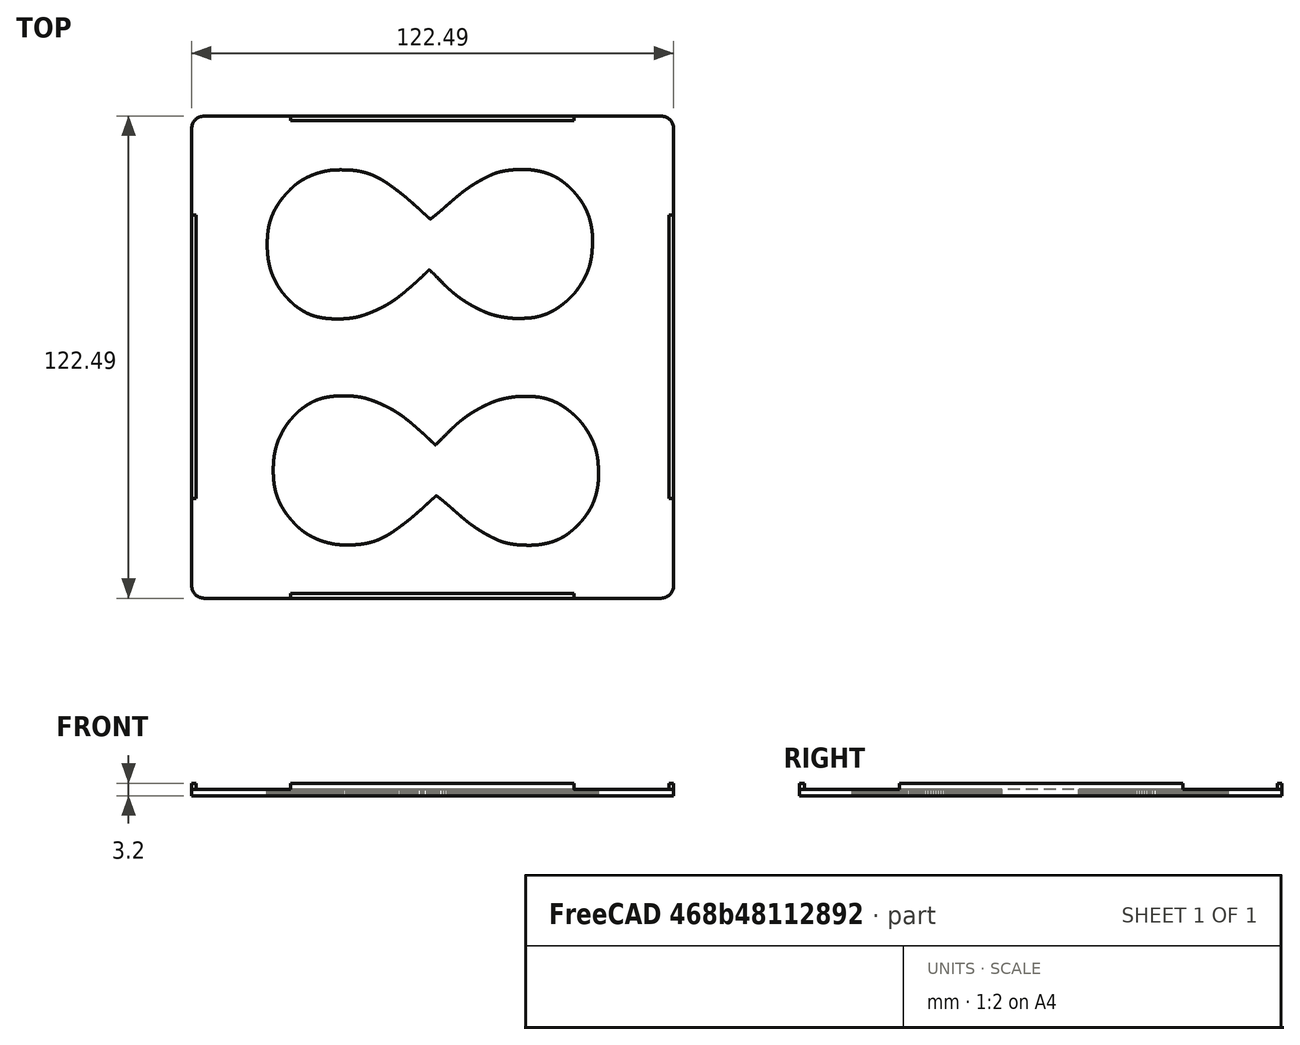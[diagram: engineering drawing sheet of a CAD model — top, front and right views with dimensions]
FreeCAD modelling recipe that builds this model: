
FCSTD DOCUMENT  (FreeCAD 0.21RUnknown)
Label: StencilCase
License: All rights reserved
LicenseURL: https://en.wikipedia.org/wiki/All_rights_reserved
objects: Part::Feature×3, Sketcher::SketchObject×3, PartDesign::Pad×2, PartDesign::Fillet×2, PartDesign::Pocket×1, PartDesign::Body×1, Mesh::Feature×1
note: 17 computed .brp shape members not serialized (recipe doc carries the construction recipe); baked Part::Feature solids carry a one-line shape summary decoded from their .brp

FEATURE [Part::Feature] rect141
  shape: bbox 120.1 x 120.1 x 2e-07 mm, 1 faces, 0 solids (baked)
FEATURE [Part::Feature] path1_5
  shape: bbox 82.66 x 37.97 x 2e-07 mm, 0 faces, 0 solids (baked)
FEATURE [Part::Feature] path1_3
  shape: bbox 82.66 x 37.97 x 2e-07 mm, 0 faces, 0 solids (baked)
FEATURE [Sketcher::SketchObject] Sketch
  FullyConstrained = false
  sketch-geometry (788):
    g0: BSplineCurve PolesCount=2 KnotsCount=2 Degree=1 IsPeriodic=0
    g1: BSplineCurve PolesCount=2 KnotsCount=2 Degree=1 IsPeriodic=0
    g2: BSplineCurve PolesCount=2 KnotsCount=2 Degree=1 IsPeriodic=0
    g3: BSplineCurve PolesCount=2 KnotsCount=2 Degree=1 IsPeriodic=0
    g4: BSplineCurve PolesCount=2 KnotsCount=2 Degree=1 IsPeriodic=0
    g5: BSplineCurve PolesCount=2 KnotsCount=2 Degree=1 IsPeriodic=0
    g6: BSplineCurve PolesCount=2 KnotsCount=2 Degree=1 IsPeriodic=0
    g7: BSplineCurve PolesCount=2 KnotsCount=2 Degree=1 IsPeriodic=0
    g8: BSplineCurve PolesCount=2 KnotsCount=2 Degree=1 IsPeriodic=0
    g9: BSplineCurve PolesCount=2 KnotsCount=2 Degree=1 IsPeriodic=0
    g10: BSplineCurve PolesCount=2 KnotsCount=2 Degree=1 IsPeriodic=0
    g11: BSplineCurve PolesCount=2 KnotsCount=2 Degree=1 IsPeriodic=0
    g12: BSplineCurve PolesCount=2 KnotsCount=2 Degree=1 IsPeriodic=0
    g13: BSplineCurve PolesCount=2 KnotsCount=2 Degree=1 IsPeriodic=0
    g14: BSplineCurve PolesCount=2 KnotsCount=2 Degree=1 IsPeriodic=0
    g15: BSplineCurve PolesCount=2 KnotsCount=2 Degree=1 IsPeriodic=0
    g16: BSplineCurve PolesCount=2 KnotsCount=2 Degree=1 IsPeriodic=0
    g17: BSplineCurve PolesCount=2 KnotsCount=2 Degree=1 IsPeriodic=0
    g18: BSplineCurve PolesCount=2 KnotsCount=2 Degree=1 IsPeriodic=0
    g19: BSplineCurve PolesCount=2 KnotsCount=2 Degree=1 IsPeriodic=0
    g20: BSplineCurve PolesCount=2 KnotsCount=2 Degree=1 IsPeriodic=0
    g21: BSplineCurve PolesCount=2 KnotsCount=2 Degree=1 IsPeriodic=0
    g22: BSplineCurve PolesCount=2 KnotsCount=2 Degree=1 IsPeriodic=0
    g23: BSplineCurve PolesCount=2 KnotsCount=2 Degree=1 IsPeriodic=0
    g24: BSplineCurve PolesCount=2 KnotsCount=2 Degree=1 IsPeriodic=0
    g25: BSplineCurve PolesCount=2 KnotsCount=2 Degree=1 IsPeriodic=0
    g26: BSplineCurve PolesCount=2 KnotsCount=2 Degree=1 IsPeriodic=0
    g27: BSplineCurve PolesCount=2 KnotsCount=2 Degree=1 IsPeriodic=0
    g28: BSplineCurve PolesCount=2 KnotsCount=2 Degree=1 IsPeriodic=0
    g29: BSplineCurve PolesCount=2 KnotsCount=2 Degree=1 IsPeriodic=0
    g30: BSplineCurve PolesCount=2 KnotsCount=2 Degree=1 IsPeriodic=0
    g31: BSplineCurve PolesCount=2 KnotsCount=2 Degree=1 IsPeriodic=0
    g32: BSplineCurve PolesCount=2 KnotsCount=2 Degree=1 IsPeriodic=0
    g33: BSplineCurve PolesCount=2 KnotsCount=2 Degree=1 IsPeriodic=0
    g34: BSplineCurve PolesCount=2 KnotsCount=2 Degree=1 IsPeriodic=0
    g35: BSplineCurve PolesCount=2 KnotsCount=2 Degree=1 IsPeriodic=0
    g36: BSplineCurve PolesCount=2 KnotsCount=2 Degree=1 IsPeriodic=0
    g37: BSplineCurve PolesCount=2 KnotsCount=2 Degree=1 IsPeriodic=0
    g38: BSplineCurve PolesCount=2 KnotsCount=2 Degree=1 IsPeriodic=0
    g39: BSplineCurve PolesCount=2 KnotsCount=2 Degree=1 IsPeriodic=0
    g40: BSplineCurve PolesCount=2 KnotsCount=2 Degree=1 IsPeriodic=0
    g41: BSplineCurve PolesCount=2 KnotsCount=2 Degree=1 IsPeriodic=0
    g42: BSplineCurve PolesCount=2 KnotsCount=2 Degree=1 IsPeriodic=0
    g43: BSplineCurve PolesCount=2 KnotsCount=2 Degree=1 IsPeriodic=0
    g44: BSplineCurve PolesCount=2 KnotsCount=2 Degree=1 IsPeriodic=0
    g45: BSplineCurve PolesCount=2 KnotsCount=2 Degree=1 IsPeriodic=0
    g46: BSplineCurve PolesCount=2 KnotsCount=2 Degree=1 IsPeriodic=0
    g47: BSplineCurve PolesCount=2 KnotsCount=2 Degree=1 IsPeriodic=0
    g48: BSplineCurve PolesCount=2 KnotsCount=2 Degree=1 IsPeriodic=0
    g49: BSplineCurve PolesCount=2 KnotsCount=2 Degree=1 IsPeriodic=0
    g50: BSplineCurve PolesCount=2 KnotsCount=2 Degree=1 IsPeriodic=0
    g51: BSplineCurve PolesCount=2 KnotsCount=2 Degree=1 IsPeriodic=0
    g52: BSplineCurve PolesCount=2 KnotsCount=2 Degree=1 IsPeriodic=0
    g53: BSplineCurve PolesCount=2 KnotsCount=2 Degree=1 IsPeriodic=0
    g54: BSplineCurve PolesCount=2 KnotsCount=2 Degree=1 IsPeriodic=0
    g55: BSplineCurve PolesCount=2 KnotsCount=2 Degree=1 IsPeriodic=0
    g56: BSplineCurve PolesCount=2 KnotsCount=2 Degree=1 IsPeriodic=0
    g57: BSplineCurve PolesCount=2 KnotsCount=2 Degree=1 IsPeriodic=0
    g58: BSplineCurve PolesCount=2 KnotsCount=2 Degree=1 IsPeriodic=0
    g59: BSplineCurve PolesCount=2 KnotsCount=2 Degree=1 IsPeriodic=0
    g60: BSplineCurve PolesCount=2 KnotsCount=2 Degree=1 IsPeriodic=0
    g61: BSplineCurve PolesCount=2 KnotsCount=2 Degree=1 IsPeriodic=0
    g62: BSplineCurve PolesCount=2 KnotsCount=2 Degree=1 IsPeriodic=0
    g63: BSplineCurve PolesCount=2 KnotsCount=2 Degree=1 IsPeriodic=0
    g64: BSplineCurve PolesCount=2 KnotsCount=2 Degree=1 IsPeriodic=0
    g65: BSplineCurve PolesCount=2 KnotsCount=2 Degree=1 IsPeriodic=0
    g66: BSplineCurve PolesCount=2 KnotsCount=2 Degree=1 IsPeriodic=0
    g67: BSplineCurve PolesCount=2 KnotsCount=2 Degree=1 IsPeriodic=0
    g68: BSplineCurve PolesCount=2 KnotsCount=2 Degree=1 IsPeriodic=0
    g69: BSplineCurve PolesCount=2 KnotsCount=2 Degree=1 IsPeriodic=0
    g70: BSplineCurve PolesCount=2 KnotsCount=2 Degree=1 IsPeriodic=0
    g71: BSplineCurve PolesCount=2 KnotsCount=2 Degree=1 IsPeriodic=0
    g72: BSplineCurve PolesCount=2 KnotsCount=2 Degree=1 IsPeriodic=0
    g73: BSplineCurve PolesCount=2 KnotsCount=2 Degree=1 IsPeriodic=0
    g74: BSplineCurve PolesCount=2 KnotsCount=2 Degree=1 IsPeriodic=0
    g75: BSplineCurve PolesCount=2 KnotsCount=2 Degree=1 IsPeriodic=0
    g76: BSplineCurve PolesCount=2 KnotsCount=2 Degree=1 IsPeriodic=0
    g77: BSplineCurve PolesCount=2 KnotsCount=2 Degree=1 IsPeriodic=0
    g78: BSplineCurve PolesCount=2 KnotsCount=2 Degree=1 IsPeriodic=0
    g79: BSplineCurve PolesCount=2 KnotsCount=2 Degree=1 IsPeriodic=0
    g80: BSplineCurve PolesCount=2 KnotsCount=2 Degree=1 IsPeriodic=0
    g81: BSplineCurve PolesCount=2 KnotsCount=2 Degree=1 IsPeriodic=0
    g82: BSplineCurve PolesCount=2 KnotsCount=2 Degree=1 IsPeriodic=0
    g83: BSplineCurve PolesCount=2 KnotsCount=2 Degree=1 IsPeriodic=0
    g84: BSplineCurve PolesCount=2 KnotsCount=2 Degree=1 IsPeriodic=0
    g85: BSplineCurve PolesCount=2 KnotsCount=2 Degree=1 IsPeriodic=0
    g86: BSplineCurve PolesCount=2 KnotsCount=2 Degree=1 IsPeriodic=0
    g87: BSplineCurve PolesCount=2 KnotsCount=2 Degree=1 IsPeriodic=0
    g88: BSplineCurve PolesCount=2 KnotsCount=2 Degree=1 IsPeriodic=0
    g89: BSplineCurve PolesCount=2 KnotsCount=2 Degree=1 IsPeriodic=0
    g90: BSplineCurve PolesCount=2 KnotsCount=2 Degree=1 IsPeriodic=0
    g91: BSplineCurve PolesCount=2 KnotsCount=2 Degree=1 IsPeriodic=0
    g92: BSplineCurve PolesCount=2 KnotsCount=2 Degree=1 IsPeriodic=0
    g93: BSplineCurve PolesCount=2 KnotsCount=2 Degree=1 IsPeriodic=0
    g94: BSplineCurve PolesCount=2 KnotsCount=2 Degree=1 IsPeriodic=0
    g95: BSplineCurve PolesCount=2 KnotsCount=2 Degree=1 IsPeriodic=0
    g96: BSplineCurve PolesCount=2 KnotsCount=2 Degree=1 IsPeriodic=0
    g97: BSplineCurve PolesCount=2 KnotsCount=2 Degree=1 IsPeriodic=0
    g98: BSplineCurve PolesCount=2 KnotsCount=2 Degree=1 IsPeriodic=0
    g99: BSplineCurve PolesCount=2 KnotsCount=2 Degree=1 IsPeriodic=0
    g100: BSplineCurve PolesCount=2 KnotsCount=2 Degree=1 IsPeriodic=0
    g101: BSplineCurve PolesCount=2 KnotsCount=2 Degree=1 IsPeriodic=0
    g102: BSplineCurve PolesCount=2 KnotsCount=2 Degree=1 IsPeriodic=0
    g103: BSplineCurve PolesCount=2 KnotsCount=2 Degree=1 IsPeriodic=0
    g104: BSplineCurve PolesCount=2 KnotsCount=2 Degree=1 IsPeriodic=0
    g105: BSplineCurve PolesCount=2 KnotsCount=2 Degree=1 IsPeriodic=0
    g106: BSplineCurve PolesCount=2 KnotsCount=2 Degree=1 IsPeriodic=0
    g107: BSplineCurve PolesCount=2 KnotsCount=2 Degree=1 IsPeriodic=0
    g108: BSplineCurve PolesCount=2 KnotsCount=2 Degree=1 IsPeriodic=0
    g109: BSplineCurve PolesCount=2 KnotsCount=2 Degree=1 IsPeriodic=0
    g110: BSplineCurve PolesCount=2 KnotsCount=2 Degree=1 IsPeriodic=0
    g111: BSplineCurve PolesCount=2 KnotsCount=2 Degree=1 IsPeriodic=0
    g112: BSplineCurve PolesCount=2 KnotsCount=2 Degree=1 IsPeriodic=0
    g113: BSplineCurve PolesCount=2 KnotsCount=2 Degree=1 IsPeriodic=0
    g114: BSplineCurve PolesCount=2 KnotsCount=2 Degree=1 IsPeriodic=0
    g115: BSplineCurve PolesCount=2 KnotsCount=2 Degree=1 IsPeriodic=0
    g116: BSplineCurve PolesCount=2 KnotsCount=2 Degree=1 IsPeriodic=0
    g117: BSplineCurve PolesCount=2 KnotsCount=2 Degree=1 IsPeriodic=0
    g118: BSplineCurve PolesCount=2 KnotsCount=2 Degree=1 IsPeriodic=0
    g119: BSplineCurve PolesCount=2 KnotsCount=2 Degree=1 IsPeriodic=0
    g120: BSplineCurve PolesCount=2 KnotsCount=2 Degree=1 IsPeriodic=0
    g121: BSplineCurve PolesCount=2 KnotsCount=2 Degree=1 IsPeriodic=0
    g122: BSplineCurve PolesCount=2 KnotsCount=2 Degree=1 IsPeriodic=0
    g123: BSplineCurve PolesCount=2 KnotsCount=2 Degree=1 IsPeriodic=0
    g124: BSplineCurve PolesCount=2 KnotsCount=2 Degree=1 IsPeriodic=0
    g125: BSplineCurve PolesCount=2 KnotsCount=2 Degree=1 IsPeriodic=0
    g126: BSplineCurve PolesCount=2 KnotsCount=2 Degree=1 IsPeriodic=0
    g127: BSplineCurve PolesCount=2 KnotsCount=2 Degree=1 IsPeriodic=0
    g128: BSplineCurve PolesCount=2 KnotsCount=2 Degree=1 IsPeriodic=0
    g129: BSplineCurve PolesCount=2 KnotsCount=2 Degree=1 IsPeriodic=0
    g130: BSplineCurve PolesCount=2 KnotsCount=2 Degree=1 IsPeriodic=0
    g131: BSplineCurve PolesCount=2 KnotsCount=2 Degree=1 IsPeriodic=0
    g132: BSplineCurve PolesCount=2 KnotsCount=2 Degree=1 IsPeriodic=0
    g133: BSplineCurve PolesCount=2 KnotsCount=2 Degree=1 IsPeriodic=0
    g134: BSplineCurve PolesCount=2 KnotsCount=2 Degree=1 IsPeriodic=0
    g135: BSplineCurve PolesCount=2 KnotsCount=2 Degree=1 IsPeriodic=0
    g136: BSplineCurve PolesCount=2 KnotsCount=2 Degree=1 IsPeriodic=0
    g137: BSplineCurve PolesCount=2 KnotsCount=2 Degree=1 IsPeriodic=0
    g138: BSplineCurve PolesCount=2 KnotsCount=2 Degree=1 IsPeriodic=0
    g139: BSplineCurve PolesCount=2 KnotsCount=2 Degree=1 IsPeriodic=0
    g140: BSplineCurve PolesCount=2 KnotsCount=2 Degree=1 IsPeriodic=0
    g141: BSplineCurve PolesCount=2 KnotsCount=2 Degree=1 IsPeriodic=0
    g142: BSplineCurve PolesCount=2 KnotsCount=2 Degree=1 IsPeriodic=0
    g143: BSplineCurve PolesCount=2 KnotsCount=2 Degree=1 IsPeriodic=0
    g144: BSplineCurve PolesCount=2 KnotsCount=2 Degree=1 IsPeriodic=0
    g145: BSplineCurve PolesCount=2 KnotsCount=2 Degree=1 IsPeriodic=0
    g146: BSplineCurve PolesCount=2 KnotsCount=2 Degree=1 IsPeriodic=0
    g147: BSplineCurve PolesCount=2 KnotsCount=2 Degree=1 IsPeriodic=0
    g148: BSplineCurve PolesCount=2 KnotsCount=2 Degree=1 IsPeriodic=0
    g149: BSplineCurve PolesCount=2 KnotsCount=2 Degree=1 IsPeriodic=0
    g150: BSplineCurve PolesCount=2 KnotsCount=2 Degree=1 IsPeriodic=0
    g151: BSplineCurve PolesCount=2 KnotsCount=2 Degree=1 IsPeriodic=0
    g152: BSplineCurve PolesCount=2 KnotsCount=2 Degree=1 IsPeriodic=0
    g153: BSplineCurve PolesCount=2 KnotsCount=2 Degree=1 IsPeriodic=0
    g154: BSplineCurve PolesCount=2 KnotsCount=2 Degree=1 IsPeriodic=0
    g155: BSplineCurve PolesCount=2 KnotsCount=2 Degree=1 IsPeriodic=0
    g156: BSplineCurve PolesCount=2 KnotsCount=2 Degree=1 IsPeriodic=0
    g157: BSplineCurve PolesCount=2 KnotsCount=2 Degree=1 IsPeriodic=0
    g158: BSplineCurve PolesCount=2 KnotsCount=2 Degree=1 IsPeriodic=0
    g159: BSplineCurve PolesCount=2 KnotsCount=2 Degree=1 IsPeriodic=0
    g160: BSplineCurve PolesCount=2 KnotsCount=2 Degree=1 IsPeriodic=0
    g161: BSplineCurve PolesCount=2 KnotsCount=2 Degree=1 IsPeriodic=0
    g162: BSplineCurve PolesCount=2 KnotsCount=2 Degree=1 IsPeriodic=0
    g163: BSplineCurve PolesCount=2 KnotsCount=2 Degree=1 IsPeriodic=0
    g164: BSplineCurve PolesCount=2 KnotsCount=2 Degree=1 IsPeriodic=0
    g165: BSplineCurve PolesCount=2 KnotsCount=2 Degree=1 IsPeriodic=0
    g166: BSplineCurve PolesCount=2 KnotsCount=2 Degree=1 IsPeriodic=0
    g167: BSplineCurve PolesCount=2 KnotsCount=2 Degree=1 IsPeriodic=0
    g168: BSplineCurve PolesCount=2 KnotsCount=2 Degree=1 IsPeriodic=0
    g169: BSplineCurve PolesCount=2 KnotsCount=2 Degree=1 IsPeriodic=0
    g170: BSplineCurve PolesCount=2 KnotsCount=2 Degree=1 IsPeriodic=0
    g171: BSplineCurve PolesCount=2 KnotsCount=2 Degree=1 IsPeriodic=0
    g172: BSplineCurve PolesCount=2 KnotsCount=2 Degree=1 IsPeriodic=0
    g173: BSplineCurve PolesCount=2 KnotsCount=2 Degree=1 IsPeriodic=0
    g174: BSplineCurve PolesCount=2 KnotsCount=2 Degree=1 IsPeriodic=0
    g175: BSplineCurve PolesCount=2 KnotsCount=2 Degree=1 IsPeriodic=0
    g176: BSplineCurve PolesCount=2 KnotsCount=2 Degree=1 IsPeriodic=0
    g177: BSplineCurve PolesCount=2 KnotsCount=2 Degree=1 IsPeriodic=0
    g178: BSplineCurve PolesCount=2 KnotsCount=2 Degree=1 IsPeriodic=0
    g179: BSplineCurve PolesCount=2 KnotsCount=2 Degree=1 IsPeriodic=0
    g180: BSplineCurve PolesCount=2 KnotsCount=2 Degree=1 IsPeriodic=0
    g181: BSplineCurve PolesCount=2 KnotsCount=2 Degree=1 IsPeriodic=0
    g182: BSplineCurve PolesCount=2 KnotsCount=2 Degree=1 IsPeriodic=0
    g183: BSplineCurve PolesCount=2 KnotsCount=2 Degree=1 IsPeriodic=0
    g184: BSplineCurve PolesCount=2 KnotsCount=2 Degree=1 IsPeriodic=0
    g185: BSplineCurve PolesCount=2 KnotsCount=2 Degree=1 IsPeriodic=0
    g186: BSplineCurve PolesCount=2 KnotsCount=2 Degree=1 IsPeriodic=0
    g187: BSplineCurve PolesCount=2 KnotsCount=2 Degree=1 IsPeriodic=0
    g188: BSplineCurve PolesCount=2 KnotsCount=2 Degree=1 IsPeriodic=0
    g189: BSplineCurve PolesCount=2 KnotsCount=2 Degree=1 IsPeriodic=0
    g190: BSplineCurve PolesCount=2 KnotsCount=2 Degree=1 IsPeriodic=0
    g191: BSplineCurve PolesCount=2 KnotsCount=2 Degree=1 IsPeriodic=0
    g192: BSplineCurve PolesCount=2 KnotsCount=2 Degree=1 IsPeriodic=0
    g193: BSplineCurve PolesCount=2 KnotsCount=2 Degree=1 IsPeriodic=0
    g194: BSplineCurve PolesCount=2 KnotsCount=2 Degree=1 IsPeriodic=0
    g195: BSplineCurve PolesCount=2 KnotsCount=2 Degree=1 IsPeriodic=0
    g196: BSplineCurve PolesCount=2 KnotsCount=2 Degree=1 IsPeriodic=0
    g197: BSplineCurve PolesCount=2 KnotsCount=2 Degree=1 IsPeriodic=0
    g198: BSplineCurve PolesCount=2 KnotsCount=2 Degree=1 IsPeriodic=0
    g199: BSplineCurve PolesCount=2 KnotsCount=2 Degree=1 IsPeriodic=0
    g200: BSplineCurve PolesCount=2 KnotsCount=2 Degree=1 IsPeriodic=0
    g201: BSplineCurve PolesCount=2 KnotsCount=2 Degree=1 IsPeriodic=0
    g202: BSplineCurve PolesCount=2 KnotsCount=2 Degree=1 IsPeriodic=0
    g203: BSplineCurve PolesCount=2 KnotsCount=2 Degree=1 IsPeriodic=0
    g204: BSplineCurve PolesCount=2 KnotsCount=2 Degree=1 IsPeriodic=0
    g205: BSplineCurve PolesCount=2 KnotsCount=2 Degree=1 IsPeriodic=0
    g206: BSplineCurve PolesCount=2 KnotsCount=2 Degree=1 IsPeriodic=0
    g207: BSplineCurve PolesCount=2 KnotsCount=2 Degree=1 IsPeriodic=0
    g208: BSplineCurve PolesCount=2 KnotsCount=2 Degree=1 IsPeriodic=0
    g209: BSplineCurve PolesCount=2 KnotsCount=2 Degree=1 IsPeriodic=0
    g210: BSplineCurve PolesCount=2 KnotsCount=2 Degree=1 IsPeriodic=0
    g211: BSplineCurve PolesCount=2 KnotsCount=2 Degree=1 IsPeriodic=0
    g212: BSplineCurve PolesCount=2 KnotsCount=2 Degree=1 IsPeriodic=0
    g213: BSplineCurve PolesCount=2 KnotsCount=2 Degree=1 IsPeriodic=0
    g214: BSplineCurve PolesCount=2 KnotsCount=2 Degree=1 IsPeriodic=0
    g215: BSplineCurve PolesCount=2 KnotsCount=2 Degree=1 IsPeriodic=0
    g216: BSplineCurve PolesCount=2 KnotsCount=2 Degree=1 IsPeriodic=0
    g217: BSplineCurve PolesCount=2 KnotsCount=2 Degree=1 IsPeriodic=0
    g218: BSplineCurve PolesCount=2 KnotsCount=2 Degree=1 IsPeriodic=0
    g219: BSplineCurve PolesCount=2 KnotsCount=2 Degree=1 IsPeriodic=0
    g220: BSplineCurve PolesCount=2 KnotsCount=2 Degree=1 IsPeriodic=0
    g221: BSplineCurve PolesCount=2 KnotsCount=2 Degree=1 IsPeriodic=0
    g222: BSplineCurve PolesCount=2 KnotsCount=2 Degree=1 IsPeriodic=0
    g223: BSplineCurve PolesCount=2 KnotsCount=2 Degree=1 IsPeriodic=0
    g224: BSplineCurve PolesCount=2 KnotsCount=2 Degree=1 IsPeriodic=0
    g225: BSplineCurve PolesCount=2 KnotsCount=2 Degree=1 IsPeriodic=0
    g226: BSplineCurve PolesCount=2 KnotsCount=2 Degree=1 IsPeriodic=0
    g227: BSplineCurve PolesCount=2 KnotsCount=2 Degree=1 IsPeriodic=0
    g228: BSplineCurve PolesCount=2 KnotsCount=2 Degree=1 IsPeriodic=0
    g229: BSplineCurve PolesCount=2 KnotsCount=2 Degree=1 IsPeriodic=0
    g230: BSplineCurve PolesCount=2 KnotsCount=2 Degree=1 IsPeriodic=0
    g231: BSplineCurve PolesCount=2 KnotsCount=2 Degree=1 IsPeriodic=0
    g232: BSplineCurve PolesCount=2 KnotsCount=2 Degree=1 IsPeriodic=0
    g233: BSplineCurve PolesCount=2 KnotsCount=2 Degree=1 IsPeriodic=0
    g234: BSplineCurve PolesCount=2 KnotsCount=2 Degree=1 IsPeriodic=0
    g235: BSplineCurve PolesCount=2 KnotsCount=2 Degree=1 IsPeriodic=0
    g236: BSplineCurve PolesCount=2 KnotsCount=2 Degree=1 IsPeriodic=0
    g237: BSplineCurve PolesCount=2 KnotsCount=2 Degree=1 IsPeriodic=0
    g238: BSplineCurve PolesCount=2 KnotsCount=2 Degree=1 IsPeriodic=0
    g239: BSplineCurve PolesCount=2 KnotsCount=2 Degree=1 IsPeriodic=0
    g240: BSplineCurve PolesCount=2 KnotsCount=2 Degree=1 IsPeriodic=0
    g241: BSplineCurve PolesCount=2 KnotsCount=2 Degree=1 IsPeriodic=0
    g242: BSplineCurve PolesCount=2 KnotsCount=2 Degree=1 IsPeriodic=0
    g243: BSplineCurve PolesCount=2 KnotsCount=2 Degree=1 IsPeriodic=0
    g244: BSplineCurve PolesCount=2 KnotsCount=2 Degree=1 IsPeriodic=0
    g245: BSplineCurve PolesCount=2 KnotsCount=2 Degree=1 IsPeriodic=0
    g246: BSplineCurve PolesCount=2 KnotsCount=2 Degree=1 IsPeriodic=0
    g247: BSplineCurve PolesCount=2 KnotsCount=2 Degree=1 IsPeriodic=0
    g248: BSplineCurve PolesCount=2 KnotsCount=2 Degree=1 IsPeriodic=0
    g249: BSplineCurve PolesCount=2 KnotsCount=2 Degree=1 IsPeriodic=0
    g250: BSplineCurve PolesCount=2 KnotsCount=2 Degree=1 IsPeriodic=0
    g251: BSplineCurve PolesCount=2 KnotsCount=2 Degree=1 IsPeriodic=0
    g252: BSplineCurve PolesCount=2 KnotsCount=2 Degree=1 IsPeriodic=0
    g253: BSplineCurve PolesCount=2 KnotsCount=2 Degree=1 IsPeriodic=0
    g254: BSplineCurve PolesCount=2 KnotsCount=2 Degree=1 IsPeriodic=0
    g255: BSplineCurve PolesCount=2 KnotsCount=2 Degree=1 IsPeriodic=0
    g256: BSplineCurve PolesCount=2 KnotsCount=2 Degree=1 IsPeriodic=0
    g257: BSplineCurve PolesCount=2 KnotsCount=2 Degree=1 IsPeriodic=0
    g258: BSplineCurve PolesCount=2 KnotsCount=2 Degree=1 IsPeriodic=0
    g259: BSplineCurve PolesCount=2 KnotsCount=2 Degree=1 IsPeriodic=0
    g260: BSplineCurve PolesCount=2 KnotsCount=2 Degree=1 IsPeriodic=0
    g261: BSplineCurve PolesCount=2 KnotsCount=2 Degree=1 IsPeriodic=0
    g262: BSplineCurve PolesCount=2 KnotsCount=2 Degree=1 IsPeriodic=0
    g263: BSplineCurve PolesCount=2 KnotsCount=2 Degree=1 IsPeriodic=0
    g264: BSplineCurve PolesCount=2 KnotsCount=2 Degree=1 IsPeriodic=0
    g265: BSplineCurve PolesCount=2 KnotsCount=2 Degree=1 IsPeriodic=0
    g266: BSplineCurve PolesCount=2 KnotsCount=2 Degree=1 IsPeriodic=0
    g267: BSplineCurve PolesCount=2 KnotsCount=2 Degree=1 IsPeriodic=0
    g268: BSplineCurve PolesCount=2 KnotsCount=2 Degree=1 IsPeriodic=0
    g269: BSplineCurve PolesCount=2 KnotsCount=2 Degree=1 IsPeriodic=0
    g270: BSplineCurve PolesCount=2 KnotsCount=2 Degree=1 IsPeriodic=0
    g271: BSplineCurve PolesCount=2 KnotsCount=2 Degree=1 IsPeriodic=0
    g272: BSplineCurve PolesCount=2 KnotsCount=2 Degree=1 IsPeriodic=0
    g273: BSplineCurve PolesCount=2 KnotsCount=2 Degree=1 IsPeriodic=0
    g274: BSplineCurve PolesCount=2 KnotsCount=2 Degree=1 IsPeriodic=0
    g275: BSplineCurve PolesCount=2 KnotsCount=2 Degree=1 IsPeriodic=0
    g276: BSplineCurve PolesCount=2 KnotsCount=2 Degree=1 IsPeriodic=0
    g277: BSplineCurve PolesCount=2 KnotsCount=2 Degree=1 IsPeriodic=0
    g278: BSplineCurve PolesCount=2 KnotsCount=2 Degree=1 IsPeriodic=0
    g279: BSplineCurve PolesCount=2 KnotsCount=2 Degree=1 IsPeriodic=0
    g280: BSplineCurve PolesCount=2 KnotsCount=2 Degree=1 IsPeriodic=0
    g281: BSplineCurve PolesCount=2 KnotsCount=2 Degree=1 IsPeriodic=0
    g282: BSplineCurve PolesCount=2 KnotsCount=2 Degree=1 IsPeriodic=0
    g283: BSplineCurve PolesCount=2 KnotsCount=2 Degree=1 IsPeriodic=0
    g284: BSplineCurve PolesCount=2 KnotsCount=2 Degree=1 IsPeriodic=0
    g285: BSplineCurve PolesCount=2 KnotsCount=2 Degree=1 IsPeriodic=0
    g286: BSplineCurve PolesCount=2 KnotsCount=2 Degree=1 IsPeriodic=0
    g287: BSplineCurve PolesCount=2 KnotsCount=2 Degree=1 IsPeriodic=0
    g288: BSplineCurve PolesCount=2 KnotsCount=2 Degree=1 IsPeriodic=0
    g289: BSplineCurve PolesCount=2 KnotsCount=2 Degree=1 IsPeriodic=0
    g290: BSplineCurve PolesCount=2 KnotsCount=2 Degree=1 IsPeriodic=0
    g291: BSplineCurve PolesCount=2 KnotsCount=2 Degree=1 IsPeriodic=0
    g292: BSplineCurve PolesCount=2 KnotsCount=2 Degree=1 IsPeriodic=0
    g293: BSplineCurve PolesCount=2 KnotsCount=2 Degree=1 IsPeriodic=0
    g294: BSplineCurve PolesCount=2 KnotsCount=2 Degree=1 IsPeriodic=0
    g295: BSplineCurve PolesCount=2 KnotsCount=2 Degree=1 IsPeriodic=0
    g296: BSplineCurve PolesCount=2 KnotsCount=2 Degree=1 IsPeriodic=0
    g297: BSplineCurve PolesCount=2 KnotsCount=2 Degree=1 IsPeriodic=0
    g298: BSplineCurve PolesCount=2 KnotsCount=2 Degree=1 IsPeriodic=0
    g299: BSplineCurve PolesCount=2 KnotsCount=2 Degree=1 IsPeriodic=0
    g300: BSplineCurve PolesCount=2 KnotsCount=2 Degree=1 IsPeriodic=0
    g301: BSplineCurve PolesCount=2 KnotsCount=2 Degree=1 IsPeriodic=0
    g302: BSplineCurve PolesCount=2 KnotsCount=2 Degree=1 IsPeriodic=0
    g303: BSplineCurve PolesCount=2 KnotsCount=2 Degree=1 IsPeriodic=0
    g304: BSplineCurve PolesCount=2 KnotsCount=2 Degree=1 IsPeriodic=0
    g305: BSplineCurve PolesCount=2 KnotsCount=2 Degree=1 IsPeriodic=0
    g306: BSplineCurve PolesCount=2 KnotsCount=2 Degree=1 IsPeriodic=0
    g307: BSplineCurve PolesCount=2 KnotsCount=2 Degree=1 IsPeriodic=0
    g308: BSplineCurve PolesCount=2 KnotsCount=2 Degree=1 IsPeriodic=0
    g309: BSplineCurve PolesCount=2 KnotsCount=2 Degree=1 IsPeriodic=0
    g310: BSplineCurve PolesCount=2 KnotsCount=2 Degree=1 IsPeriodic=0
    g311: BSplineCurve PolesCount=2 KnotsCount=2 Degree=1 IsPeriodic=0
    g312: BSplineCurve PolesCount=2 KnotsCount=2 Degree=1 IsPeriodic=0
    g313: BSplineCurve PolesCount=2 KnotsCount=2 Degree=1 IsPeriodic=0
    g314: BSplineCurve PolesCount=2 KnotsCount=2 Degree=1 IsPeriodic=0
    g315: BSplineCurve PolesCount=2 KnotsCount=2 Degree=1 IsPeriodic=0
    g316: BSplineCurve PolesCount=2 KnotsCount=2 Degree=1 IsPeriodic=0
    g317: BSplineCurve PolesCount=2 KnotsCount=2 Degree=1 IsPeriodic=0
    g318: BSplineCurve PolesCount=2 KnotsCount=2 Degree=1 IsPeriodic=0
    g319: BSplineCurve PolesCount=2 KnotsCount=2 Degree=1 IsPeriodic=0
    g320: BSplineCurve PolesCount=2 KnotsCount=2 Degree=1 IsPeriodic=0
    g321: BSplineCurve PolesCount=2 KnotsCount=2 Degree=1 IsPeriodic=0
    g322: BSplineCurve PolesCount=2 KnotsCount=2 Degree=1 IsPeriodic=0
    g323: BSplineCurve PolesCount=2 KnotsCount=2 Degree=1 IsPeriodic=0
    g324: BSplineCurve PolesCount=2 KnotsCount=2 Degree=1 IsPeriodic=0
    g325: BSplineCurve PolesCount=2 KnotsCount=2 Degree=1 IsPeriodic=0
    g326: BSplineCurve PolesCount=2 KnotsCount=2 Degree=1 IsPeriodic=0
    g327: BSplineCurve PolesCount=2 KnotsCount=2 Degree=1 IsPeriodic=0
    g328: BSplineCurve PolesCount=2 KnotsCount=2 Degree=1 IsPeriodic=0
    g329: BSplineCurve PolesCount=2 KnotsCount=2 Degree=1 IsPeriodic=0
    g330: BSplineCurve PolesCount=2 KnotsCount=2 Degree=1 IsPeriodic=0
    g331: BSplineCurve PolesCount=2 KnotsCount=2 Degree=1 IsPeriodic=0
    g332: BSplineCurve PolesCount=2 KnotsCount=2 Degree=1 IsPeriodic=0
    g333: BSplineCurve PolesCount=2 KnotsCount=2 Degree=1 IsPeriodic=0
    g334: BSplineCurve PolesCount=2 KnotsCount=2 Degree=1 IsPeriodic=0
    g335: BSplineCurve PolesCount=2 KnotsCount=2 Degree=1 IsPeriodic=0
    g336: BSplineCurve PolesCount=2 KnotsCount=2 Degree=1 IsPeriodic=0
    g337: BSplineCurve PolesCount=2 KnotsCount=2 Degree=1 IsPeriodic=0
    g338: BSplineCurve PolesCount=2 KnotsCount=2 Degree=1 IsPeriodic=0
    g339: BSplineCurve PolesCount=2 KnotsCount=2 Degree=1 IsPeriodic=0
    g340: BSplineCurve PolesCount=2 KnotsCount=2 Degree=1 IsPeriodic=0
    g341: BSplineCurve PolesCount=2 KnotsCount=2 Degree=1 IsPeriodic=0
    g342: BSplineCurve PolesCount=2 KnotsCount=2 Degree=1 IsPeriodic=0
    g343: BSplineCurve PolesCount=2 KnotsCount=2 Degree=1 IsPeriodic=0
    g344: BSplineCurve PolesCount=2 KnotsCount=2 Degree=1 IsPeriodic=0
    g345: BSplineCurve PolesCount=2 KnotsCount=2 Degree=1 IsPeriodic=0
    g346: BSplineCurve PolesCount=2 KnotsCount=2 Degree=1 IsPeriodic=0
    g347: BSplineCurve PolesCount=2 KnotsCount=2 Degree=1 IsPeriodic=0
    g348: BSplineCurve PolesCount=2 KnotsCount=2 Degree=1 IsPeriodic=0
    g349: BSplineCurve PolesCount=2 KnotsCount=2 Degree=1 IsPeriodic=0
    g350: BSplineCurve PolesCount=2 KnotsCount=2 Degree=1 IsPeriodic=0
    g351: BSplineCurve PolesCount=2 KnotsCount=2 Degree=1 IsPeriodic=0
    g352: BSplineCurve PolesCount=2 KnotsCount=2 Degree=1 IsPeriodic=0
    g353: BSplineCurve PolesCount=2 KnotsCount=2 Degree=1 IsPeriodic=0
    g354: BSplineCurve PolesCount=2 KnotsCount=2 Degree=1 IsPeriodic=0
    g355: BSplineCurve PolesCount=2 KnotsCount=2 Degree=1 IsPeriodic=0
    g356: BSplineCurve PolesCount=2 KnotsCount=2 Degree=1 IsPeriodic=0
    g357: BSplineCurve PolesCount=2 KnotsCount=2 Degree=1 IsPeriodic=0
    g358: BSplineCurve PolesCount=2 KnotsCount=2 Degree=1 IsPeriodic=0
    g359: BSplineCurve PolesCount=2 KnotsCount=2 Degree=1 IsPeriodic=0
    g360: BSplineCurve PolesCount=2 KnotsCount=2 Degree=1 IsPeriodic=0
    g361: BSplineCurve PolesCount=2 KnotsCount=2 Degree=1 IsPeriodic=0
    g362: BSplineCurve PolesCount=2 KnotsCount=2 Degree=1 IsPeriodic=0
    g363: BSplineCurve PolesCount=2 KnotsCount=2 Degree=1 IsPeriodic=0
    g364: BSplineCurve PolesCount=2 KnotsCount=2 Degree=1 IsPeriodic=0
    g365: BSplineCurve PolesCount=2 KnotsCount=2 Degree=1 IsPeriodic=0
    g366: BSplineCurve PolesCount=2 KnotsCount=2 Degree=1 IsPeriodic=0
    g367: BSplineCurve PolesCount=2 KnotsCount=2 Degree=1 IsPeriodic=0
    g368: BSplineCurve PolesCount=2 KnotsCount=2 Degree=1 IsPeriodic=0
    g369: BSplineCurve PolesCount=2 KnotsCount=2 Degree=1 IsPeriodic=0
    g370: BSplineCurve PolesCount=2 KnotsCount=2 Degree=1 IsPeriodic=0
    g371: BSplineCurve PolesCount=2 KnotsCount=2 Degree=1 IsPeriodic=0
    g372: BSplineCurve PolesCount=2 KnotsCount=2 Degree=1 IsPeriodic=0
    g373: BSplineCurve PolesCount=2 KnotsCount=2 Degree=1 IsPeriodic=0
    g374: BSplineCurve PolesCount=2 KnotsCount=2 Degree=1 IsPeriodic=0
    g375: BSplineCurve PolesCount=2 KnotsCount=2 Degree=1 IsPeriodic=0
    g376: BSplineCurve PolesCount=2 KnotsCount=2 Degree=1 IsPeriodic=0
    g377: BSplineCurve PolesCount=2 KnotsCount=2 Degree=1 IsPeriodic=0
    g378: BSplineCurve PolesCount=2 KnotsCount=2 Degree=1 IsPeriodic=0
    g379: BSplineCurve PolesCount=2 KnotsCount=2 Degree=1 IsPeriodic=0
    g380: BSplineCurve PolesCount=2 KnotsCount=2 Degree=1 IsPeriodic=0
    g381: BSplineCurve PolesCount=2 KnotsCount=2 Degree=1 IsPeriodic=0
    g382: BSplineCurve PolesCount=2 KnotsCount=2 Degree=1 IsPeriodic=0
    g383: BSplineCurve PolesCount=2 KnotsCount=2 Degree=1 IsPeriodic=0
    g384: BSplineCurve PolesCount=2 KnotsCount=2 Degree=1 IsPeriodic=0
    g385: BSplineCurve PolesCount=2 KnotsCount=2 Degree=1 IsPeriodic=0
    g386: BSplineCurve PolesCount=2 KnotsCount=2 Degree=1 IsPeriodic=0
    g387: BSplineCurve PolesCount=2 KnotsCount=2 Degree=1 IsPeriodic=0
    g388: BSplineCurve PolesCount=2 KnotsCount=2 Degree=1 IsPeriodic=0
    g389: BSplineCurve PolesCount=2 KnotsCount=2 Degree=1 IsPeriodic=0
    g390: BSplineCurve PolesCount=2 KnotsCount=2 Degree=1 IsPeriodic=0
    g391: BSplineCurve PolesCount=2 KnotsCount=2 Degree=1 IsPeriodic=0
    g392: BSplineCurve PolesCount=2 KnotsCount=2 Degree=1 IsPeriodic=0
    g393: BSplineCurve PolesCount=2 KnotsCount=2 Degree=1 IsPeriodic=0
    g394: BSplineCurve PolesCount=2 KnotsCount=2 Degree=1 IsPeriodic=0
    g395: BSplineCurve PolesCount=2 KnotsCount=2 Degree=1 IsPeriodic=0
    g396: BSplineCurve PolesCount=2 KnotsCount=2 Degree=1 IsPeriodic=0
    g397: BSplineCurve PolesCount=2 KnotsCount=2 Degree=1 IsPeriodic=0
    g398: BSplineCurve PolesCount=2 KnotsCount=2 Degree=1 IsPeriodic=0
    g399: BSplineCurve PolesCount=2 KnotsCount=2 Degree=1 IsPeriodic=0
    ... +388 more geometry lines
  constraints (788):
    c: Coincident(g0,g1)
    c: Coincident(g1,g2)
    c: Coincident(g2,g3)
    c: Coincident(g3,g0)
    c: Coincident(g4,g5)
    c: Coincident(g5,g6)
    c: Coincident(g6,g7)
    c: Coincident(g7,g8)
    c: Coincident(g8,g9)
    c: Coincident(g9,g10)
    c: Coincident(g10,g11)
    c: Coincident(g11,g12)
    c: Coincident(g12,g13)
    c: Coincident(g13,g14)
    c: Coincident(g14,g15)
    c: Coincident(g15,g16)
    c: Coincident(g16,g17)
    c: Coincident(g17,g18)
    c: Coincident(g18,g19)
    c: Coincident(g19,g20)
    c: Coincident(g20,g21)
    c: Coincident(g21,g22)
    c: Coincident(g22,g23)
    c: Coincident(g23,g24)
    c: Coincident(g24,g25)
    c: Coincident(g25,g26)
    c: Coincident(g26,g27)
    c: Coincident(g27,g28)
    c: Coincident(g28,g29)
    c: Coincident(g29,g30)
    c: Coincident(g30,g31)
    c: Coincident(g31,g32)
    c: Coincident(g32,g33)
    c: Coincident(g33,g34)
    c: Coincident(g34,g35)
    c: Coincident(g35,g36)
    c: Coincident(g36,g37)
    c: Coincident(g37,g38)
    c: Coincident(g38,g39)
    c: Coincident(g39,g40)
    c: Coincident(g40,g41)
    c: Coincident(g41,g42)
    c: Coincident(g42,g43)
    c: Coincident(g43,g44)
    c: Coincident(g44,g45)
    c: Coincident(g45,g46)
    c: Coincident(g46,g47)
    c: Coincident(g47,g48)
    c: Coincident(g48,g49)
    c: Coincident(g49,g50)
    c: Coincident(g50,g51)
    c: Coincident(g51,g52)
    c: Coincident(g52,g53)
    c: Coincident(g53,g54)
    c: Coincident(g54,g55)
    c: Coincident(g55,g56)
    c: Coincident(g56,g57)
    c: Coincident(g57,g58)
    c: Coincident(g58,g59)
    c: Coincident(g59,g60)
    c: Coincident(g60,g61)
    c: Coincident(g61,g62)
    c: Coincident(g62,g63)
    c: Coincident(g63,g64)
    c: Coincident(g64,g65)
    c: Coincident(g65,g66)
    c: Coincident(g66,g67)
    c: Coincident(g67,g68)
    c: Coincident(g68,g69)
    c: Coincident(g69,g70)
    c: Coincident(g70,g71)
    c: Coincident(g71,g72)
    c: Coincident(g72,g73)
    c: Coincident(g73,g74)
    c: Coincident(g74,g75)
    c: Coincident(g75,g76)
    c: Coincident(g76,g77)
    c: Coincident(g77,g78)
    c: Coincident(g78,g79)
    c: Coincident(g79,g80)
    c: Coincident(g80,g81)
    c: Coincident(g81,g82)
    c: Coincident(g82,g83)
    c: Coincident(g83,g84)
    c: Coincident(g84,g85)
    c: Coincident(g85,g86)
    c: Coincident(g86,g87)
    c: Coincident(g87,g88)
    c: Coincident(g88,g89)
    c: Coincident(g89,g90)
    c: Coincident(g90,g91)
    c: Coincident(g91,g92)
    c: Coincident(g92,g93)
    c: Coincident(g93,g94)
    c: Coincident(g94,g95)
    c: Coincident(g95,g96)
    c: Coincident(g96,g97)
    c: Coincident(g97,g98)
    c: Coincident(g98,g99)
    c: Coincident(g99,g100)
    c: Coincident(g100,g101)
    c: Coincident(g101,g102)
    c: Coincident(g102,g103)
    c: Coincident(g103,g104)
    c: Coincident(g104,g105)
    c: Coincident(g105,g106)
    c: Coincident(g106,g107)
    c: Coincident(g107,g108)
    c: Coincident(g108,g109)
    c: Coincident(g109,g110)
    c: Coincident(g110,g111)
    c: Coincident(g111,g112)
    c: Coincident(g112,g113)
    c: Coincident(g113,g114)
    c: Coincident(g114,g115)
    c: Coincident(g115,g116)
    c: Coincident(g116,g117)
    c: Coincident(g117,g118)
    c: Coincident(g118,g119)
    c: Coincident(g119,g120)
    c: Coincident(g120,g121)
    c: Coincident(g121,g122)
    c: Coincident(g122,g123)
    c: Coincident(g123,g124)
    c: Coincident(g124,g125)
    c: Coincident(g125,g126)
    c: Coincident(g126,g127)
    c: Coincident(g127,g128)
    c: Coincident(g128,g129)
    c: Coincident(g129,g130)
    c: Coincident(g130,g131)
    c: Coincident(g131,g132)
    c: Coincident(g132,g133)
    c: Coincident(g133,g134)
    c: Coincident(g134,g135)
    c: Coincident(g135,g136)
    c: Coincident(g136,g137)
    c: Coincident(g137,g138)
    c: Coincident(g138,g139)
    c: Coincident(g139,g140)
    c: Coincident(g140,g141)
    c: Coincident(g141,g142)
    c: Coincident(g142,g143)
    c: Coincident(g143,g144)
    c: Coincident(g144,g145)
    c: Coincident(g145,g146)
    c: Coincident(g146,g147)
    c: Coincident(g147,g148)
    c: Coincident(g148,g149)
    c: Coincident(g149,g150)
    c: Coincident(g150,g151)
    c: Coincident(g151,g152)
    c: Coincident(g152,g153)
    c: Coincident(g153,g154)
    c: Coincident(g154,g155)
    c: Coincident(g155,g156)
    c: Coincident(g156,g157)
    c: Coincident(g157,g158)
    c: Coincident(g158,g159)
    c: Coincident(g159,g160)
    c: Coincident(g160,g161)
    c: Coincident(g161,g162)
    c: Coincident(g162,g163)
    c: Coincident(g163,g164)
    c: Coincident(g164,g165)
    c: Coincident(g165,g166)
    c: Coincident(g166,g167)
    c: Coincident(g167,g168)
    c: Coincident(g168,g169)
    c: Coincident(g169,g170)
    c: Coincident(g170,g171)
    c: Coincident(g171,g172)
    c: Coincident(g172,g173)
    c: Coincident(g173,g174)
    c: Coincident(g174,g175)
    c: Coincident(g175,g176)
    c: Coincident(g176,g177)
    c: Coincident(g177,g178)
    c: Coincident(g178,g179)
    c: Coincident(g179,g180)
    c: Coincident(g180,g181)
    c: Coincident(g181,g182)
    c: Coincident(g182,g183)
    c: Coincident(g183,g184)
    c: Coincident(g184,g185)
    c: Coincident(g185,g186)
    c: Coincident(g186,g187)
    c: Coincident(g187,g188)
    c: Coincident(g188,g189)
    c: Coincident(g189,g190)
    c: Coincident(g190,g191)
    c: Coincident(g191,g192)
    c: Coincident(g192,g193)
    c: Coincident(g193,g194)
    c: Coincident(g194,g195)
    c: Coincident(g195,g196)
    c: Coincident(g196,g197)
    c: Coincident(g197,g198)
    c: Coincident(g198,g199)
    c: Coincident(g199,g200)
    c: Coincident(g200,g201)
    c: Coincident(g201,g202)
    c: Coincident(g202,g203)
    c: Coincident(g203,g204)
    c: Coincident(g204,g205)
    c: Coincident(g205,g206)
    c: Coincident(g206,g207)
    c: Coincident(g207,g208)
    c: Coincident(g208,g209)
    c: Coincident(g209,g210)
    c: Coincident(g210,g211)
    c: Coincident(g211,g212)
    c: Coincident(g212,g213)
    c: Coincident(g213,g214)
    c: Coincident(g214,g215)
    c: Coincident(g215,g216)
    c: Coincident(g216,g217)
    c: Coincident(g217,g218)
    c: Coincident(g218,g219)
    c: Coincident(g219,g220)
    c: Coincident(g220,g221)
    c: Coincident(g221,g222)
    c: Coincident(g222,g223)
    c: Coincident(g223,g224)
    c: Coincident(g224,g225)
    c: Coincident(g225,g226)
    c: Coincident(g226,g227)
    c: Coincident(g227,g228)
    c: Coincident(g228,g229)
    c: Coincident(g229,g230)
    c: Coincident(g230,g231)
    c: Coincident(g231,g232)
    c: Coincident(g232,g233)
    c: Coincident(g233,g234)
    c: Coincident(g234,g235)
    c: Coincident(g235,g236)
    c: Coincident(g236,g237)
    c: Coincident(g237,g238)
    c: Coincident(g238,g239)
    c: Coincident(g239,g240)
    c: Coincident(g240,g241)
    c: Coincident(g241,g242)
    c: Coincident(g242,g243)
    c: Coincident(g243,g244)
    c: Coincident(g244,g245)
    c: Coincident(g245,g246)
    c: Coincident(g246,g247)
    c: Coincident(g247,g248)
    c: Coincident(g248,g249)
    c: Coincident(g249,g250)
    c: Coincident(g250,g251)
    c: Coincident(g251,g252)
    c: Coincident(g252,g253)
    c: Coincident(g253,g254)
    c: Coincident(g254,g255)
    c: Coincident(g255,g256)
    c: Coincident(g256,g257)
    c: Coincident(g257,g258)
    c: Coincident(g258,g259)
    c: Coincident(g259,g260)
    c: Coincident(g260,g261)
    c: Coincident(g261,g262)
    c: Coincident(g262,g263)
    c: Coincident(g263,g264)
    c: Coincident(g264,g265)
    c: Coincident(g265,g266)
    c: Coincident(g266,g267)
    c: Coincident(g267,g268)
    c: Coincident(g268,g269)
    c: Coincident(g269,g270)
    c: Coincident(g270,g271)
    c: Coincident(g271,g272)
    c: Coincident(g272,g273)
    c: Coincident(g273,g274)
    c: Coincident(g274,g275)
    c: Coincident(g275,g276)
    c: Coincident(g276,g277)
    c: Coincident(g277,g278)
    c: Coincident(g278,g279)
    c: Coincident(g279,g280)
    c: Coincident(g280,g281)
    c: Coincident(g281,g282)
    c: Coincident(g282,g283)
    c: Coincident(g283,g284)
    c: Coincident(g284,g285)
    c: Coincident(g285,g286)
    c: Coincident(g286,g287)
    c: Coincident(g287,g288)
    c: Coincident(g288,g289)
    c: Coincident(g289,g290)
    c: Coincident(g290,g291)
    c: Coincident(g291,g292)
    c: Coincident(g292,g293)
    c: Coincident(g293,g294)
    c: Coincident(g294,g295)
    c: Coincident(g295,g296)
    c: Coincident(g296,g297)
    c: Coincident(g297,g298)
    c: Coincident(g298,g299)
    c: Coincident(g299,g300)
    c: Coincident(g300,g301)
    c: Coincident(g301,g302)
    c: Coincident(g302,g303)
    c: Coincident(g303,g304)
    c: Coincident(g304,g305)
    c: Coincident(g305,g306)
    c: Coincident(g306,g307)
    c: Coincident(g307,g308)
    c: Coincident(g308,g309)
    c: Coincident(g309,g310)
    c: Coincident(g310,g311)
    c: Coincident(g311,g312)
    c: Coincident(g312,g313)
    c: Coincident(g313,g314)
    c: Coincident(g314,g315)
    c: Coincident(g315,g316)
    c: Coincident(g316,g317)
    c: Coincident(g317,g318)
    c: Coincident(g318,g319)
    c: Coincident(g319,g320)
    c: Coincident(g320,g321)
    c: Coincident(g321,g322)
    c: Coincident(g322,g323)
    c: Coincident(g323,g324)
    c: Coincident(g324,g325)
    c: Coincident(g325,g326)
    c: Coincident(g326,g327)
    c: Coincident(g327,g328)
    c: Coincident(g328,g329)
    c: Coincident(g329,g330)
    c: Coincident(g330,g331)
    c: Coincident(g331,g332)
    c: Coincident(g332,g333)
    c: Coincident(g333,g334)
    c: Coincident(g334,g335)
    c: Coincident(g335,g336)
    c: Coincident(g336,g337)
    c: Coincident(g337,g338)
    c: Coincident(g338,g339)
    c: Coincident(g339,g340)
    c: Coincident(g340,g341)
    c: Coincident(g341,g342)
    c: Coincident(g342,g343)
    c: Coincident(g343,g344)
    c: Coincident(g344,g345)
    c: Coincident(g345,g346)
    c: Coincident(g346,g347)
    c: Coincident(g347,g348)
    c: Coincident(g348,g349)
    c: Coincident(g349,g350)
    c: Coincident(g350,g351)
    c: Coincident(g351,g352)
    c: Coincident(g352,g353)
    c: Coincident(g353,g354)
    c: Coincident(g354,g355)
    c: Coincident(g355,g356)
    c: Coincident(g356,g357)
    c: Coincident(g357,g358)
    c: Coincident(g358,g359)
    c: Coincident(g359,g360)
    c: Coincident(g360,g361)
    c: Coincident(g361,g362)
    c: Coincident(g362,g363)
    c: Coincident(g363,g364)
    c: Coincident(g364,g365)
    c: Coincident(g365,g366)
    c: Coincident(g366,g367)
    c: Coincident(g367,g368)
    c: Coincident(g368,g369)
    c: Coincident(g369,g370)
    c: Coincident(g370,g371)
    c: Coincident(g371,g372)
    c: Coincident(g372,g373)
    c: Coincident(g373,g374)
    c: Coincident(g374,g375)
    c: Coincident(g375,g376)
    c: Coincident(g376,g377)
    c: Coincident(g377,g378)
    c: Coincident(g378,g379)
    c: Coincident(g379,g380)
    c: Coincident(g380,g381)
    c: Coincident(g381,g382)
    c: Coincident(g382,g383)
    c: Coincident(g383,g384)
    c: Coincident(g384,g385)
    c: Coincident(g385,g386)
    c: Coincident(g386,g387)
    c: Coincident(g387,g388)
    c: Coincident(g388,g389)
    c: Coincident(g389,g390)
    c: Coincident(g390,g391)
    c: Coincident(g391,g392)
    c: Coincident(g392,g393)
    c: Coincident(g393,g394)
    c: Coincident(g394,g395)
    c: Coincident(g395,g4)
    c: Coincident(g396,g397)
    c: Coincident(g397,g398)
    c: Coincident(g398,g399)
    c: Coincident(g399,g400)
    c: Coincident(g400,g401)
    c: Coincident(g401,g402)
    c: Coincident(g402,g403)
    c: Coincident(g403,g404)
    c: Coincident(g404,g405)
    c: Coincident(g405,g406)
    c: Coincident(g406,g407)
    c: Coincident(g407,g408)
    c: Coincident(g408,g409)
    c: Coincident(g409,g410)
    c: Coincident(g410,g411)
    c: Coincident(g411,g412)
    c: Coincident(g412,g413)
    c: Coincident(g413,g414)
    c: Coincident(g414,g415)
    c: Coincident(g415,g416)
    c: Coincident(g416,g417)
    c: Coincident(g417,g418)
    c: Coincident(g418,g419)
    c: Coincident(g419,g420)
    c: Coincident(g420,g421)
    c: Coincident(g421,g422)
    c: Coincident(g422,g423)
    c: Coincident(g423,g424)
    c: Coincident(g424,g425)
    c: Coincident(g425,g426)
    c: Coincident(g426,g427)
    c: Coincident(g427,g428)
    c: Coincident(g428,g429)
    c: Coincident(g429,g430)
    c: Coincident(g430,g431)
    c: Coincident(g431,g432)
    c: Coincident(g432,g433)
    c: Coincident(g433,g434)
    c: Coincident(g434,g435)
    c: Coincident(g435,g436)
    c: Coincident(g436,g437)
    c: Coincident(g437,g438)
    c: Coincident(g438,g439)
    c: Coincident(g439,g440)
    c: Coincident(g440,g441)
    c: Coincident(g441,g442)
    c: Coincident(g442,g443)
    c: Coincident(g443,g444)
    c: Coincident(g444,g445)
    c: Coincident(g445,g446)
    c: Coincident(g446,g447)
    c: Coincident(g447,g448)
    c: Coincident(g448,g449)
    c: Coincident(g449,g450)
    c: Coincident(g450,g451)
    c: Coincident(g451,g452)
    c: Coincident(g452,g453)
    c: Coincident(g453,g454)
    c: Coincident(g454,g455)
    c: Coincident(g455,g456)
    c: Coincident(g456,g457)
    c: Coincident(g457,g458)
    c: Coincident(g458,g459)
    c: Coincident(g459,g460)
    c: Coincident(g460,g461)
    c: Coincident(g461,g462)
    c: Coincident(g462,g463)
    c: Coincident(g463,g464)
    c: Coincident(g464,g465)
    c: Coincident(g465,g466)
    c: Coincident(g466,g467)
    c: Coincident(g467,g468)
    c: Coincident(g468,g469)
    c: Coincident(g469,g470)
    c: Coincident(g470,g471)
    c: Coincident(g471,g472)
    c: Coincident(g472,g473)
    c: Coincident(g473,g474)
    c: Coincident(g474,g475)
    c: Coincident(g475,g476)
    c: Coincident(g476,g477)
    c: Coincident(g477,g478)
    c: Coincident(g478,g479)
    c: Coincident(g479,g480)
    c: Coincident(g480,g481)
    c: Coincident(g481,g482)
    c: Coincident(g482,g483)
    c: Coincident(g483,g484)
    c: Coincident(g484,g485)
    c: Coincident(g485,g486)
    c: Coincident(g486,g487)
    c: Coincident(g487,g488)
    c: Coincident(g488,g489)
    c: Coincident(g489,g490)
    c: Coincident(g490,g491)
    c: Coincident(g491,g492)
    c: Coincident(g492,g493)
    c: Coincident(g493,g494)
    c: Coincident(g494,g495)
    c: Coincident(g495,g496)
    c: Coincident(g496,g497)
    c: Coincident(g497,g498)
    c: Coincident(g498,g499)
    c: Coincident(g499,g500)
    c: Coincident(g500,g501)
    c: Coincident(g501,g502)
    c: Coincident(g502,g503)
    c: Coincident(g503,g504)
    c: Coincident(g504,g505)
    c: Coincident(g505,g506)
    c: Coincident(g506,g507)
    c: Coincident(g507,g508)
    c: Coincident(g508,g509)
    c: Coincident(g509,g510)
    c: Coincident(g510,g511)
    c: Coincident(g511,g512)
    c: Coincident(g512,g513)
    c: Coincident(g513,g514)
    c: Coincident(g514,g515)
    c: Coincident(g515,g516)
    c: Coincident(g516,g517)
    c: Coincident(g517,g518)
    c: Coincident(g518,g519)
    c: Coincident(g519,g520)
    c: Coincident(g520,g521)
    c: Coincident(g521,g522)
    c: Coincident(g522,g523)
    c: Coincident(g523,g524)
    c: Coincident(g524,g525)
    c: Coincident(g525,g526)
    c: Coincident(g526,g527)
    c: Coincident(g527,g528)
    c: Coincident(g528,g529)
    c: Coincident(g529,g530)
    c: Coincident(g530,g531)
    c: Coincident(g531,g532)
    c: Coincident(g532,g533)
    c: Coincident(g533,g534)
    c: Coincident(g534,g535)
    c: Coincident(g535,g536)
    c: Coincident(g536,g537)
    c: Coincident(g537,g538)
    c: Coincident(g538,g539)
    c: Coincident(g539,g540)
    c: Coincident(g540,g541)
    c: Coincident(g541,g542)
    c: Coincident(g542,g543)
    c: Coincident(g543,g544)
    c: Coincident(g544,g545)
    c: Coincident(g545,g546)
    c: Coincident(g546,g547)
    c: Coincident(g547,g548)
    c: Coincident(g548,g549)
    c: Coincident(g549,g550)
    c: Coincident(g550,g551)
    c: Coincident(g551,g552)
    c: Coincident(g552,g553)
    c: Coincident(g553,g554)
    c: Coincident(g554,g555)
    c: Coincident(g555,g556)
    c: Coincident(g556,g557)
    c: Coincident(g557,g558)
    c: Coincident(g558,g559)
    c: Coincident(g559,g560)
    c: Coincident(g560,g561)
    c: Coincident(g561,g562)
    c: Coincident(g562,g563)
    c: Coincident(g563,g564)
    c: Coincident(g564,g565)
    c: Coincident(g565,g566)
    c: Coincident(g566,g567)
    c: Coincident(g567,g568)
    c: Coincident(g568,g569)
    c: Coincident(g569,g570)
    c: Coincident(g570,g571)
    c: Coincident(g571,g572)
    c: Coincident(g572,g573)
    c: Coincident(g573,g574)
    c: Coincident(g574,g575)
    c: Coincident(g575,g576)
    c: Coincident(g576,g577)
    c: Coincident(g577,g578)
    c: Coincident(g578,g579)
    c: Coincident(g579,g580)
    c: Coincident(g580,g581)
    c: Coincident(g581,g582)
    c: Coincident(g582,g583)
    c: Coincident(g583,g584)
    c: Coincident(g584,g585)
    c: Coincident(g585,g586)
    c: Coincident(g586,g587)
    c: Coincident(g587,g588)
    c: Coincident(g588,g589)
    c: Coincident(g589,g590)
    c: Coincident(g590,g591)
    c: Coincident(g591,g592)
    c: Coincident(g592,g593)
    c: Coincident(g593,g594)
    c: Coincident(g594,g595)
    c: Coincident(g595,g596)
    c: Coincident(g596,g597)
    c: Coincident(g597,g598)
    c: Coincident(g598,g599)
    c: Coincident(g599,g600)
    c: Coincident(g600,g601)
    c: Coincident(g601,g602)
    c: Coincident(g602,g603)
    c: Coincident(g603,g604)
    c: Coincident(g604,g605)
    c: Coincident(g605,g606)
    c: Coincident(g606,g607)
    c: Coincident(g607,g608)
    c: Coincident(g608,g609)
    c: Coincident(g609,g610)
    c: Coincident(g610,g611)
    c: Coincident(g611,g612)
    c: Coincident(g612,g613)
    c: Coincident(g613,g614)
    c: Coincident(g614,g615)
    c: Coincident(g615,g616)
    c: Coincident(g616,g617)
    c: Coincident(g617,g618)
    c: Coincident(g618,g619)
    c: Coincident(g619,g620)
    c: Coincident(g620,g621)
    c: Coincident(g621,g622)
    c: Coincident(g622,g623)
    c: Coincident(g623,g624)
    c: Coincident(g624,g625)
    c: Coincident(g625,g626)
    c: Coincident(g626,g627)
    c: Coincident(g627,g628)
    c: Coincident(g628,g629)
    c: Coincident(g629,g630)
    c: Coincident(g630,g631)
    c: Coincident(g631,g632)
    c: Coincident(g632,g633)
    c: Coincident(g633,g634)
    c: Coincident(g634,g635)
    c: Coincident(g635,g636)
    c: Coincident(g636,g637)
    c: Coincident(g637,g638)
    c: Coincident(g638,g639)
    c: Coincident(g639,g640)
    c: Coincident(g640,g641)
    c: Coincident(g641,g642)
    c: Coincident(g642,g643)
    c: Coincident(g643,g644)
    c: Coincident(g644,g645)
    c: Coincident(g645,g646)
    c: Coincident(g646,g647)
    c: Coincident(g647,g648)
    c: Coincident(g648,g649)
    c: Coincident(g649,g650)
    c: Coincident(g650,g651)
    c: Coincident(g651,g652)
    c: Coincident(g652,g653)
    c: Coincident(g653,g654)
    c: Coincident(g654,g655)
    c: Coincident(g655,g656)
    c: Coincident(g656,g657)
    c: Coincident(g657,g658)
    c: Coincident(g658,g659)
    c: Coincident(g659,g660)
    c: Coincident(g660,g661)
    c: Coincident(g661,g662)
    c: Coincident(g662,g663)
    c: Coincident(g663,g664)
    c: Coincident(g664,g665)
    c: Coincident(g665,g666)
    c: Coincident(g666,g667)
    c: Coincident(g667,g668)
    c: Coincident(g668,g669)
    c: Coincident(g669,g670)
    c: Coincident(g670,g671)
    c: Coincident(g671,g672)
    c: Coincident(g672,g673)
    c: Coincident(g673,g674)
    c: Coincident(g674,g675)
    c: Coincident(g675,g676)
    c: Coincident(g676,g677)
    c: Coincident(g677,g678)
    c: Coincident(g678,g679)
    c: Coincident(g679,g680)
    c: Coincident(g680,g681)
    c: Coincident(g681,g682)
    c: Coincident(g682,g683)
    c: Coincident(g683,g684)
    c: Coincident(g684,g685)
    c: Coincident(g685,g686)
    c: Coincident(g686,g687)
    c: Coincident(g687,g688)
    c: Coincident(g688,g689)
    c: Coincident(g689,g690)
    c: Coincident(g690,g691)
    c: Coincident(g691,g692)
    c: Coincident(g692,g693)
    c: Coincident(g693,g694)
    c: Coincident(g694,g695)
    c: Coincident(g695,g696)
    c: Coincident(g696,g697)
    c: Coincident(g697,g698)
    c: Coincident(g698,g699)
    c: Coincident(g699,g700)
    c: Coincident(g700,g701)
    c: Coincident(g701,g702)
    c: Coincident(g702,g703)
    c: Coincident(g703,g704)
    c: Coincident(g704,g705)
    c: Coincident(g705,g706)
    c: Coincident(g706,g707)
    c: Coincident(g707,g708)
    c: Coincident(g708,g709)
    c: Coincident(g709,g710)
    c: Coincident(g710,g711)
    c: Coincident(g711,g712)
    c: Coincident(g712,g713)
    c: Coincident(g713,g714)
    c: Coincident(g714,g715)
    c: Coincident(g715,g716)
    c: Coincident(g716,g717)
    c: Coincident(g717,g718)
    c: Coincident(g718,g719)
    c: Coincident(g719,g720)
    c: Coincident(g720,g721)
    c: Coincident(g721,g722)
    c: Coincident(g722,g723)
    c: Coincident(g723,g724)
    c: Coincident(g724,g725)
    c: Coincident(g725,g726)
    c: Coincident(g726,g727)
    c: Coincident(g727,g728)
    c: Coincident(g728,g729)
    c: Coincident(g729,g730)
    c: Coincident(g730,g731)
    c: Coincident(g731,g732)
    c: Coincident(g732,g733)
    c: Coincident(g733,g734)
    c: Coincident(g734,g735)
    c: Coincident(g735,g736)
    c: Coincident(g736,g737)
    c: Coincident(g737,g738)
    c: Coincident(g738,g739)
    c: Coincident(g739,g740)
    c: Coincident(g740,g741)
    c: Coincident(g741,g742)
    c: Coincident(g742,g743)
    c: Coincident(g743,g744)
    c: Coincident(g744,g745)
    c: Coincident(g745,g746)
    c: Coincident(g746,g747)
    c: Coincident(g747,g748)
    c: Coincident(g748,g749)
    c: Coincident(g749,g750)
    c: Coincident(g750,g751)
    c: Coincident(g751,g752)
    c: Coincident(g752,g753)
    c: Coincident(g753,g754)
    c: Coincident(g754,g755)
    c: Coincident(g755,g756)
    c: Coincident(g756,g757)
    c: Coincident(g757,g758)
    c: Coincident(g758,g759)
    c: Coincident(g759,g760)
    c: Coincident(g760,g761)
    c: Coincident(g761,g762)
    c: Coincident(g762,g763)
    c: Coincident(g763,g764)
    c: Coincident(g764,g765)
    c: Coincident(g765,g766)
    c: Coincident(g766,g767)
    c: Coincident(g767,g768)
    c: Coincident(g768,g769)
    c: Coincident(g769,g770)
    c: Coincident(g770,g771)
    c: Coincident(g771,g772)
    c: Coincident(g772,g773)
    c: Coincident(g773,g774)
    c: Coincident(g774,g775)
    c: Coincident(g775,g776)
    c: Coincident(g776,g777)
    c: Coincident(g777,g778)
    c: Coincident(g778,g779)
    c: Coincident(g779,g780)
    c: Coincident(g780,g781)
    c: Coincident(g781,g782)
    c: Coincident(g782,g783)
    c: Coincident(g783,g784)
    c: Coincident(g784,g785)
    c: Coincident(g785,g786)
    c: Coincident(g786,g787)
    c: Coincident(g787,g396)
FEATURE [PartDesign::Pad] Pad
  Direction = (0,0,1)
  Length = 1.6
  Length2 = 10
  Profile = -> Sketch
  ReferenceAxis = -> Sketch [N_Axis]
  Type = 0
FEATURE [Sketcher::SketchObject] Sketch001
  ExternalGeometry = -> [Pad]
  FullyConstrained = true
  MapMode = 5
  Placement = pos=(0,0,1.6) rot=(0,0,1;0rad)
  Support = -> [Pad]
  sketch-geometry (8):
    g0: LineSegment StartX=0 StartY=0 StartZ=0 EndX=120.089 EndY=0 EndZ=0
    g1: LineSegment StartX=120.089 StartY=0 StartZ=0 EndX=120.089 EndY=-120.089 EndZ=0
    g2: LineSegment StartX=120.089 StartY=-120.089 StartZ=0 EndX=0 EndY=-120.089 EndZ=0
    g3: LineSegment StartX=0 StartY=-120.089 StartZ=0 EndX=0 EndY=0 EndZ=0
    g4: LineSegment StartX=-1.2 StartY=1.2 StartZ=0 EndX=121.289 EndY=1.2 EndZ=0
    g5: LineSegment StartX=121.289 StartY=1.2 StartZ=0 EndX=121.289 EndY=-121.289 EndZ=0
    g6: LineSegment StartX=121.289 StartY=-121.289 StartZ=0 EndX=-1.2 EndY=-121.289 EndZ=0
    g7: LineSegment StartX=-1.2 StartY=-121.289 StartZ=0 EndX=-1.2 EndY=1.2 EndZ=0
  constraints (22):
    c: Coincident(g0,g1)
    c: Coincident(g1,g2)
    c: Coincident(g2,g3)
    c: Coincident(g3,g0)
    c: Horizontal(g0)
    c: Horizontal(g2)
    c: Vertical(g1)
    c: Vertical(g3)
    c: Coincident(g0,g-1)
    c: Coincident(g4,g5)
    c: Coincident(g5,g6)
    c: Coincident(g6,g7)
    c: Coincident(g7,g4)
    c: Horizontal(g4)
    c: Horizontal(g6)
    c: Vertical(g5)
    c: Vertical(g7)
    c: Coincident(g1,g-3)
    c: DistanceY(g5,g1) = 1.2
    c: DistanceX(g1,g5) = 1.2
    c: DistanceX(g4,g0) = 1.2
    c: DistanceY(g0,g4) = 1.2
FEATURE [PartDesign::Pad] Pad001
  BaseFeature = -> Pad
  Direction = (0,0,1)
  Length = 1.6
  Length2 = 1.6
  Profile = -> Sketch001
  ReferenceAxis = -> Sketch001 [N_Axis]
  Type = 4
FEATURE [PartDesign::Fillet] Fillet
  Base = -> Pad001 [Edge2367,Edge2365,Edge2370,Edge2368]
  BaseFeature = -> Pad001
  Radius = 2
  SupportTransform = false
  UseAllEdges = false
FEATURE [PartDesign::Fillet] Fillet001
  Base = -> Fillet [Edge2390,Edge2385,Edge2386,Edge2388]
  BaseFeature = -> Fillet
  Radius = 3.2
  SupportTransform = false
  UseAllEdges = false
FEATURE [Sketcher::SketchObject] Sketch002
  FullyConstrained = true
  MapMode = 5
  Placement = pos=(0,0,3.2) rot=(0,0,1;0rad)
  Support = -> [Fillet001]
  sketch-geometry (16):
    g0: LineSegment StartX=-2 StartY=2 StartZ=0 EndX=24 EndY=2 EndZ=0
    g1: LineSegment StartX=24 StartY=2 StartZ=0 EndX=24 EndY=-24 EndZ=0
    g2: LineSegment StartX=24 StartY=-24 StartZ=0 EndX=-2 EndY=-24 EndZ=0
    g3: LineSegment StartX=-2 StartY=-24 StartZ=0 EndX=-2 EndY=2 EndZ=0
    g4: LineSegment StartX=122 StartY=2 StartZ=0 EndX=96 EndY=2 EndZ=0
    g5: LineSegment StartX=96 StartY=2 StartZ=0 EndX=96 EndY=-24 EndZ=0
    g6: LineSegment StartX=96 StartY=-24 StartZ=0 EndX=122 EndY=-24 EndZ=0
    g7: LineSegment StartX=122 StartY=-24 StartZ=0 EndX=122 EndY=2 EndZ=0
    g8: LineSegment StartX=122 StartY=-122 StartZ=0 EndX=96 EndY=-122 EndZ=0
    g9: LineSegment StartX=96 StartY=-122 StartZ=0 EndX=96 EndY=-96 EndZ=0
    g10: LineSegment StartX=96 StartY=-96 StartZ=0 EndX=122 EndY=-96 EndZ=0
    g11: LineSegment StartX=122 StartY=-96 StartZ=0 EndX=122 EndY=-122 EndZ=0
    g12: LineSegment StartX=-2 StartY=-122 StartZ=0 EndX=24 EndY=-122 EndZ=0
    g13: LineSegment StartX=24 StartY=-122 StartZ=0 EndX=24 EndY=-96 EndZ=0
    g14: LineSegment StartX=24 StartY=-96 StartZ=0 EndX=-2 EndY=-96 EndZ=0
    g15: LineSegment StartX=-2 StartY=-96 StartZ=0 EndX=-2 EndY=-122 EndZ=0
  constraints (48):
    c: Coincident(g0,g1)
    c: Coincident(g1,g2)
    c: Coincident(g2,g3)
    c: Coincident(g3,g0)
    c: Horizontal(g0)
    c: Horizontal(g2)
    c: Vertical(g1)
    c: Vertical(g3)
    c: Coincident(g4,g5)
    c: Coincident(g5,g6)
    c: Coincident(g6,g7)
    c: Coincident(g7,g4)
    c: Horizontal(g4)
    c: Horizontal(g6)
    c: Vertical(g5)
    c: Vertical(g7)
    c: Coincident(g8,g9)
    c: Coincident(g9,g10)
    c: Coincident(g10,g11)
    c: Coincident(g11,g8)
    c: Horizontal(g8)
    c: Horizontal(g10)
    c: Vertical(g9)
    c: Vertical(g11)
    c: Coincident(g12,g13)
    c: Coincident(g13,g14)
    c: Coincident(g14,g15)
    c: Coincident(g15,g12)
    c: Horizontal(g12)
    c: Horizontal(g14)
    c: Vertical(g13)
    c: Vertical(g15)
    c: Equal(g14,g0)
    c: Equal(g15,g3)
    c: Equal(g0,g4)
    c: Equal(g5,g3)
    c: Equal(g7,g11)
    c: Equal(g6,g10)
    c: DistanceX(g0,g-1) = 2
    c: DistanceY(g-1,g0) = 2
    c: DistanceY(g2,g-1) = 24
    c: DistanceX(g-1,g0) = 24
    c: DistanceX(g-1,g4) = 122
    c: Horizontal(g0,g4)
    c: Horizontal(g13,g9)
    c: Vertical(g14,g2)
    c: DistanceY(g12,g-1) = 122
    c: Vertical(g10,g6)
FEATURE [PartDesign::Pocket] Pocket
  BaseFeature = -> Fillet001
  Direction = (0,0,-1)
  Length = 0
  Length2 = 5
  Profile = -> Sketch002
  ReferenceAxis = -> Sketch002 [N_Axis]
  Type = 3
  UpToFace = -> Fillet001 [Face19]
FEATURE [PartDesign::Body] Body  label="StencilCase"
  Group = -> [Sketch,Pad,Sketch001,Pad001,Fillet,Fillet001,Sketch002,Pocket]
  Origin = -> Origin
  Tip = -> Pocket
FEATURE [Mesh::Feature] Mesh  label="StencilCase (Meshed)"
